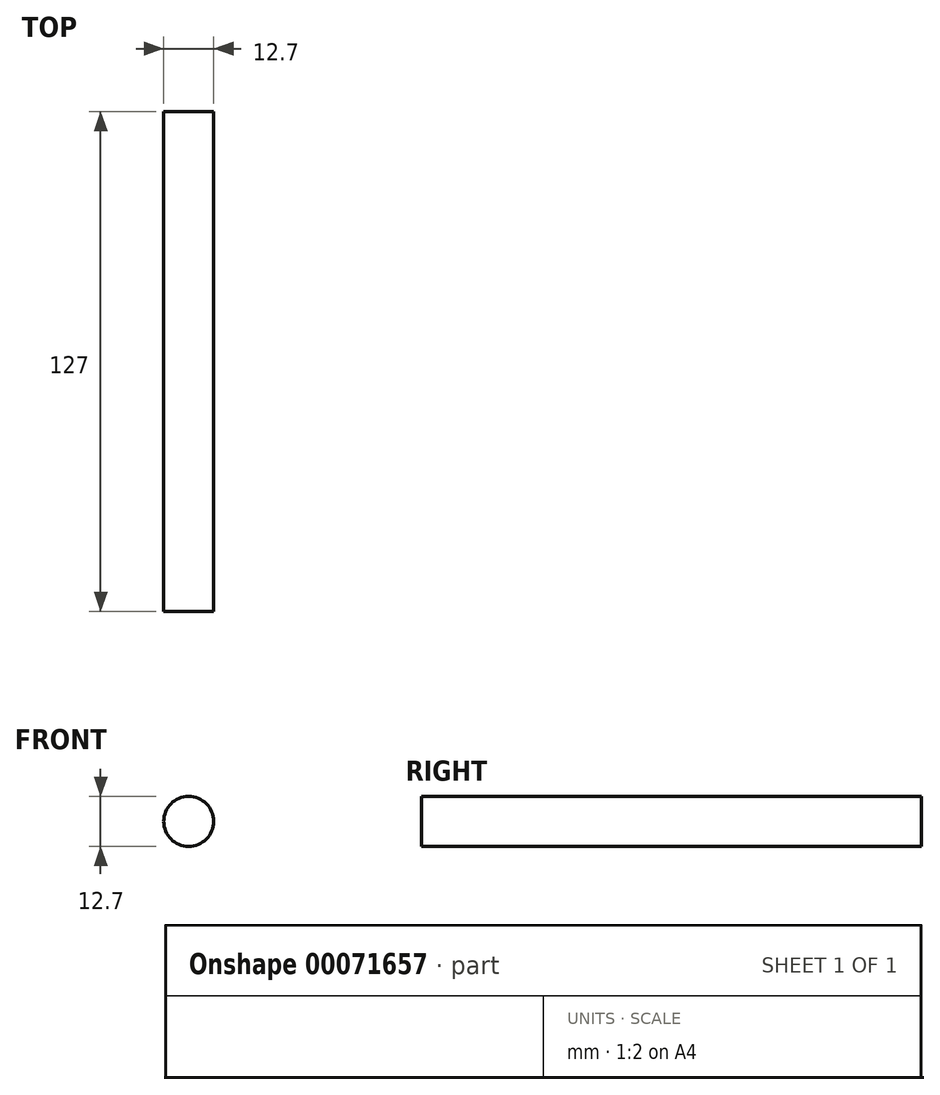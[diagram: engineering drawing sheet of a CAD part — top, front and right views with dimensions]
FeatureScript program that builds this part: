
annotation { "Feature Type Name" : "Feature", "Feature Type Description" : "" }
export const myFeature = defineFeature(function(context is Context, id is Id, definition is map)
    precondition{}
    {
        {
            var Q0;
            Q0=qCreatedBy(makeId("Front.planeOp"),FACE);
            var sketch = newSketch(context, id + "F0", { "sketchPlane" : qUnion([Q0])});
            skCircle(sketch, "E0", {"center": v(-65.53, 47.06) * mm, "radius": 6.35 * mm});
            skSolve(sketch);
        }
        {
            var Q0;
            Q0=makeQuery(id+"F0.imprint","IMPRINT",FACE,{"disambiguationData":[TD([[makeQuery(id+"F0.imprint","IMPRINT",EDGE,{"derivedFrom":sQuery(id+"F0.wireOp",EDGE,"E0")}),1.0]])]});
            extrude(context, id + "F1", {"entities" : qUnion([Q0]), "depth" : 127 * mm});
        }
    });
